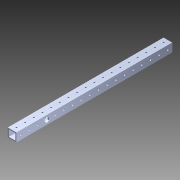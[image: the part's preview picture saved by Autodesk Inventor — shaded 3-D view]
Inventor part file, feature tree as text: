
AUTODESK INVENTOR PART (.ipt)
format: ipt  version: 2014 (Build 180170000, 170)  size: 1,286,144 bytes
history: native  units: in
note: dims shown in document units (in); Inventor stores cm internally (conversion verified against a paired STEP export)
features: extrude x2, sketch x2, pattern_circular x1, other x1, plane x1, imported_body x1
ambient origin geometry x8: Origin, YZ Plane, XZ Plane, XY Plane, X Axis, Y Axis, Z Axis, Center Point
bodies: Body1 (feature_tree)
feature tree (8):
  pattern_circular  "CirPattern2"
  other  "217-3426-STEP1"
  plane  "Work Plane1"
  extrude  "Extrusion1"  Depth=3937.0079in TaperAngle=0.0deg
  sketch  "Sketch3"  dims[d3=0.5in d5=2.0in d6=0.0in d7=0.5938in]
  extrude  "Extrusion2"  Depth=0.5in TaperAngle=0.0deg
  imported_body  "Base1"
  sketch  "Sketch1"  dims[d0=-18.0in d1=3937.0079in d2=0.0in]
